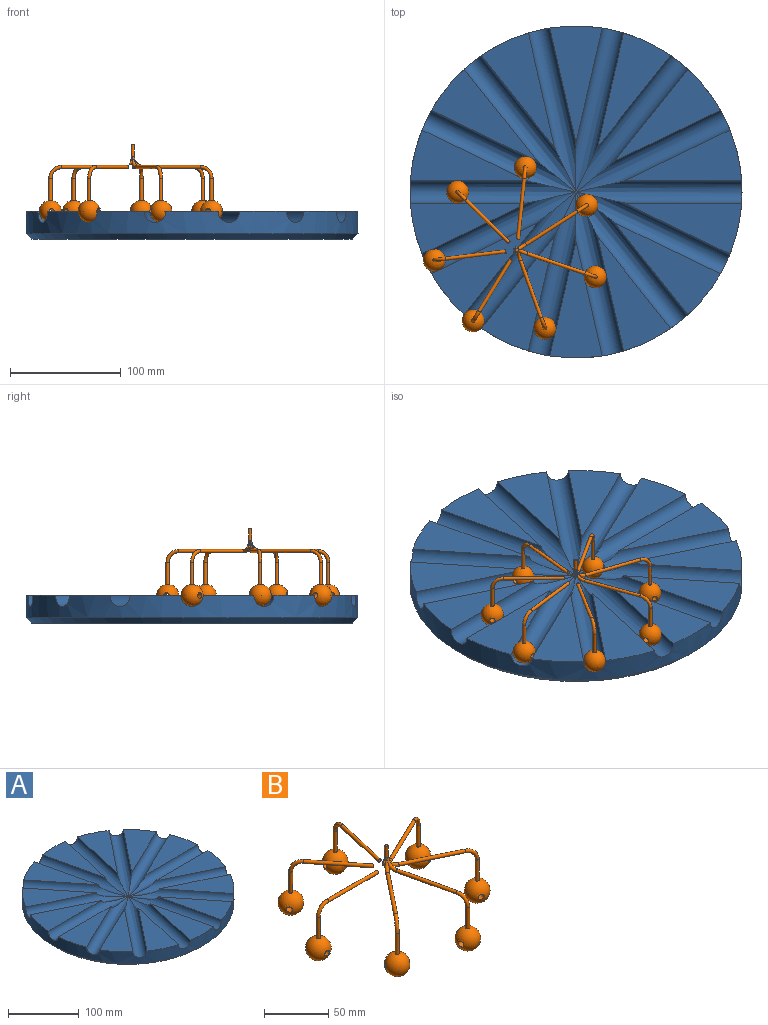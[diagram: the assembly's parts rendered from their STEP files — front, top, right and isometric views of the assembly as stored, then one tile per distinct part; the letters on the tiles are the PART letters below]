
ASSEMBLY  parts=2 mates=1
PART A: 31 faces, bbox 300x300x25 mm
  f0: plane 105.85x45.93mm, normal (0,0,1), area 2489.3mm2, adj f14,f17,f29
  f1: plane 95.37x82.76mm, normal (0,0,1), area 2489.3mm2, adj f14,f27,f28
  f2: plane 95.37x82.76mm, normal (0,0,1), area 2489.3mm2, adj f14,f26,f29
  f3: plane 103.2x66mm, normal (0,0,1), area 2489.3mm2, adj f14,f24,f27
  f4: plane 103.2x66mm, normal (0,0,1), area 2489.3mm2, adj f14,f25,f26
  f5: plane 105.06x47.11mm, normal (0,0,1), area 2489.3mm2, adj f14,f23,f24
  f6: plane 105.06x47.11mm, normal (0,0,1), area 2489.3mm2, adj f14,f22,f25
  f7: plane 103.2x66mm, normal (0,0,1), area 2489.3mm2, adj f14,f20,f23
  f8: plane 103.2x66mm, normal (0,0,1), area 2489.3mm2, adj f14,f21,f22
  f9: plane 95.37x82.76mm, normal (0,0,1), area 2489.3mm2, adj f14,f19,f20
  f10: plane 95.37x82.76mm, normal (0,0,1), area 2489.3mm2, adj f14,f18,f21
  f11: plane 105.85x45.93mm, normal (0,0,1), area 2489.3mm2, adj f14,f17,f19
  f12: cylinder r=10mm len=150mm, axis (1,0,0), area 3830.9mm2, adj f13,f14,f15,f18,f28
  f13: plane 105.85x45.93mm, normal (0,0,1), area 2489.3mm2, adj f12,f14,f18
  f14: cylinder r=150mm len=300mm, axis (0,0,-1), area 16657.5mm2, adj f0,f1,f2,f3,f4,f5,f6,f7
  f15: plane 105.85x45.93mm, normal (0,0,1), area 2489.3mm2, adj f12,f14,f28
  f16: plane 290x290mm, normal (0,0,-1), area 66052mm2, adj f30
  f17: cylinder r=10mm len=150mm, axis (1,0,0), area 3830.9mm2, adj f0,f11,f14,f19,f29
  f18: cylinder r=10mm len=143.82mm, axis (0.9,-0.43,0), area 3830.9mm2, adj f10,f12,f13,f14,f21
  f19: cylinder r=10mm len=143.82mm, axis (0.9,-0.43,0), area 3830.9mm2, adj f9,f11,f14,f17,f20
  f20: cylinder r=10mm len=129.74mm, axis (0.62,-0.78,0), area 3830.9mm2, adj f7,f9,f14,f19,f23
  f21: cylinder r=10mm len=129.74mm, axis (0.62,-0.78,0), area 3830.9mm2, adj f8,f10,f14,f18,f22
  f22: cylinder r=10mm len=150.69mm, axis (0.22,-0.97,0), area 3830.9mm2, adj f6,f8,f14,f21,f25
  f23: cylinder r=10mm len=150.69mm, axis (0.22,-0.97,0), area 3830.9mm2, adj f5,f7,f14,f20,f24
  f24: cylinder r=10mm len=150.69mm, axis (-0.22,-0.97,0), area 3830.9mm2, adj f3,f5,f14,f23,f27
  f25: cylinder r=10mm len=150.69mm, axis (-0.22,-0.97,0), area 3830.9mm2, adj f4,f6,f14,f22,f26
  f26: cylinder r=10mm len=129.74mm, axis (-0.62,-0.78,0), area 3830.9mm2, adj f2,f4,f14,f25,f29
  f27: cylinder r=10mm len=129.74mm, axis (-0.62,-0.78,0), area 3830.9mm2, adj f1,f3,f14,f24,f28
  f28: cylinder r=10mm len=143.82mm, axis (-0.9,-0.43,0), area 3830.9mm2, adj f1,f12,f14,f15,f27
  f29: cylinder r=10mm len=143.82mm, axis (-0.9,-0.43,0), area 3830.9mm2, adj f0,f2,f14,f17,f26
  f30: cone r=150mm half-angle=45deg, axis (0,0,1), area 6553.3mm2, adj f14,f16
PART B: 48 faces, bbox 162.6x166.2x70 mm
  f0: sphere r=10mm, area 1209.6mm2, adj f1,f2
  f1: cylinder r=2.5mm len=19.37mm, axis (0,1,0), area 304.2mm2, adj f0
  f2: cylinder r=1.5mm len=20.11mm, axis (0,0,-1), area 189.6mm2, adj f0,f3
  f3: torus R=10mm, axis (0,-1,0), area 148mm2, adj f2,f4
  f4: cylinder r=1.5mm len=55mm, axis (-1,0,0), area 518.4mm2, adj f3,f5
  f5: torus R=10mm, axis (0,1,0), area 0mm2, adj f4
  f6: plane 3x3mm, normal (0,0,1), area 7.1mm2, adj f7
  f7: cylinder r=1.5mm len=10mm, axis (0,0,-1), area 94.2mm2, adj f6,f8,f9,f10,f11,f12,f13,f14
  f8: torus R=10mm, axis (-0.43,-0.9,0), area 91mm2, adj f7,f9,f14,f15
  f9: torus R=10mm, axis (0.43,-0.9,0), area 56.9mm2, adj f7,f8,f10
  f10: torus R=10mm, axis (0.97,-0.22,0), area 57mm2, adj f7,f9,f11
  f11: torus R=10mm, axis (0.78,0.62,0), area 56.9mm2, adj f7,f10,f12
  f12: torus R=10mm, axis (0,1,0), area 57mm2, adj f7,f11,f13
  f13: torus R=10mm, axis (-0.78,0.62,0), area 91mm2, adj f7,f12,f14,f16
  f14: torus R=10mm, axis (-0.97,-0.22,0), area 91mm2, adj f7,f8,f13,f17
  f15: cylinder r=1.5mm len=50.86mm, axis (0.9,-0.43,0), area 518.4mm2, adj f8,f18
  f16: cylinder r=1.5mm len=44.87mm, axis (-0.62,-0.78,0), area 518.4mm2, adj f13,f19
  f17: cylinder r=1.5mm len=54.29mm, axis (0.22,-0.97,0), area 518.4mm2, adj f14,f20
  f18: torus R=10mm, axis (0.43,0.9,0), area 148mm2, adj f15,f21
  f19: torus R=10mm, axis (0.78,-0.62,0), area 148mm2, adj f16,f22
  f20: torus R=10mm, axis (0.97,0.22,0), area 148mm2, adj f17,f23
  f21: cylinder r=1.5mm len=20.11mm, axis (0,0,-1), area 189.6mm2, adj f18,f24
  f22: cylinder r=1.5mm len=20.11mm, axis (0,0,-1), area 189.6mm2, adj f19,f25
  f23: cylinder r=1.5mm len=20.11mm, axis (0,0,-1), area 189.6mm2, adj f20,f26
  f24: sphere r=10mm, area 1209.6mm2, adj f21,f27
  f25: sphere r=10mm, area 1209.6mm2, adj f22,f28
  f26: sphere r=10mm, area 1209.6mm2, adj f23,f29
  f27: cylinder r=2.5mm len=19.62mm, axis (-0.43,-0.9,0), area 304.2mm2, adj f24
  f28: cylinder r=2.5mm len=18.26mm, axis (-0.78,0.62,0), area 304.2mm2, adj f25
  f29: cylinder r=2.5mm len=19.99mm, axis (-0.97,-0.22,0), area 304.2mm2, adj f26
  f30: sphere r=10mm, area 1209.6mm2, adj f31,f32
  f31: cylinder r=2.5mm len=18.26mm, axis (0.78,0.62,0), area 304.2mm2, adj f30
  f32: cylinder r=1.5mm len=20.11mm, axis (0,0,-1), area 189.6mm2, adj f30,f33
  f33: torus R=10mm, axis (-0.78,-0.62,0), area 148mm2, adj f32,f34
  f34: cylinder r=1.5mm len=44.87mm, axis (-0.62,0.78,0), area 518.4mm2, adj f33,f35
  f35: torus R=10mm, axis (0.78,0.62,0), area 0mm2, adj f34
  f36: sphere r=10mm, area 1209.6mm2, adj f37,f38
  f37: cylinder r=2.5mm len=19.99mm, axis (0.97,-0.22,0), area 304.2mm2, adj f36
  f38: cylinder r=1.5mm len=20.11mm, axis (0,0,-1), area 189.6mm2, adj f36,f39
  f39: torus R=10mm, axis (-0.97,0.22,0), area 148mm2, adj f38,f40
  f40: cylinder r=1.5mm len=54.29mm, axis (0.22,0.97,0), area 518.4mm2, adj f39,f41
  f41: torus R=10mm, axis (0.97,-0.22,0), area 0mm2, adj f40
  f42: sphere r=10mm, area 1209.6mm2, adj f43,f44
  f43: cylinder r=2.5mm len=19.62mm, axis (0.43,-0.9,0), area 304.2mm2, adj f42
  f44: cylinder r=1.5mm len=20.11mm, axis (0,0,-1), area 189.6mm2, adj f42,f45
  f45: torus R=10mm, axis (-0.43,0.9,0), area 148mm2, adj f44,f46
  f46: cylinder r=1.5mm len=50.86mm, axis (0.9,0.43,0), area 518.4mm2, adj f45,f47
  f47: torus R=10mm, axis (0.43,-0.9,0), area 0mm2, adj f46
PLACE A t=(0.54,-0.15,-13.48)mm fixed
PLACE B rot(axis=(0,0,1),58.4deg) t=(-52.95,-52.72,-38.48)mm
MATE parallel B.f7 <-> A.f14  axis (0,0,1) through (-52.95,-52.72,71.52)mm
